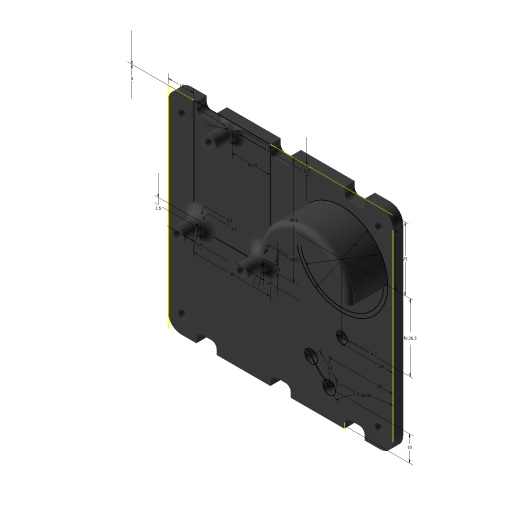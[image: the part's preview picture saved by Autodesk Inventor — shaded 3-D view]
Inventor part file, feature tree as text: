
AUTODESK INVENTOR PART (.ipt)
format: ipt  version: 2023 (Build 270158000, 158)  size: 345,600 bytes
history: native  units: mm
features: extrude x8, sketch x6, fillet x4, projected_geometry x1
ambient origin geometry x8: Origin, YZ Plane, XZ Plane, XY Plane, X Axis, Y Axis, Z Axis, Center Point
bodies: Solid1 (feature_tree)
feature tree (19):
  extrude  "Extrusion1"  Depth=82.0mm
  sketch  "Sketch2"  dims[d2=3.2mm d3=3.2mm d4=3.2mm]
  extrude  "Extrusion2"  Depth=3.2mm
  fillet  "Fillet1"  Radius=3.2mm
  extrude  "Extrusion3"  Depth=77.0mm
  fillet  "Fillet2"  Radius=68.0mm
  extrude  "Extrusion4"  Depth=5.5mm
  extrude  "Extrusion5"  Depth=7.0mm
  fillet  "Fillet3"  Radius=5.5mm
  sketch  "Sketch5"  dims[d10=7.0mm d11=7.0mm d12=5.5mm]
  extrude  "Extrusion6"  Depth=4.0mm TaperAngle=0.0deg
  extrude  "Extrusion7"  Depth=2.0mm
  extrude  "Extrusion8"  Depth=2.0mm
  fillet  "Fillet4"  Radius=10.0mm
  sketch  "Sketch1"  dims[d0=88.0mm d1=82.0mm]
  sketch  "Sketch3"  dims[d5=3.2mm d6=77.0mm d7=68.0mm]
  sketch  "Sketch4"  dims[d8=7.0mm d9=5.5mm]
  sketch  "Sketch6"  dims[d13=5.5mm d14=4.0mm d15=0.0mm d16=30.0mm d17=42.5mm d18=10.0mm d19=0.0mm d20=3.2mm d21=3.2mm d22=3.2mm d23=2.6mm d24=2.5mm d25=2.5mm d26=2.5mm d27=2.5mm d28=15.0mm d29=5.2mm d30=5.2mm d31=5.2mm d32=9.0mm d33=0.0mm d34=4.0mm d35=4.2mm d36=4.2mm d37=4.2mm d38=3.5mm d39=0.0mm d40=3.0mm d41=0.0mm d42=0.0mm d43=8.0mm d44=4.0mm d45=0.0mm d46=40.0mm d47=88.0mm d48=8.0mm d49=4.0mm d50=8.0mm d51=4.0mm d52=21.0mm d53=21.0mm d54=2.0mm d55=0.0mm d56=0.0mm d57=5.0mm d58=33.0mm d59=36.0mm d60=4.2mm d61=26.5mm d62=20.0mm d63=25.0mm d64=25.0mm d65=5.0mm d66=5.0mm d67=45.0deg d68=10.0mm d69=25.0mm d70=10.0mm d71=0.0mm d72=0.0mm d73=15.0mm d74=0.0mm d75=5.0mm d76=2.0mm d77=0.0mm d78=2.0mm]
  projected_geometry  "Projected Loop1"
